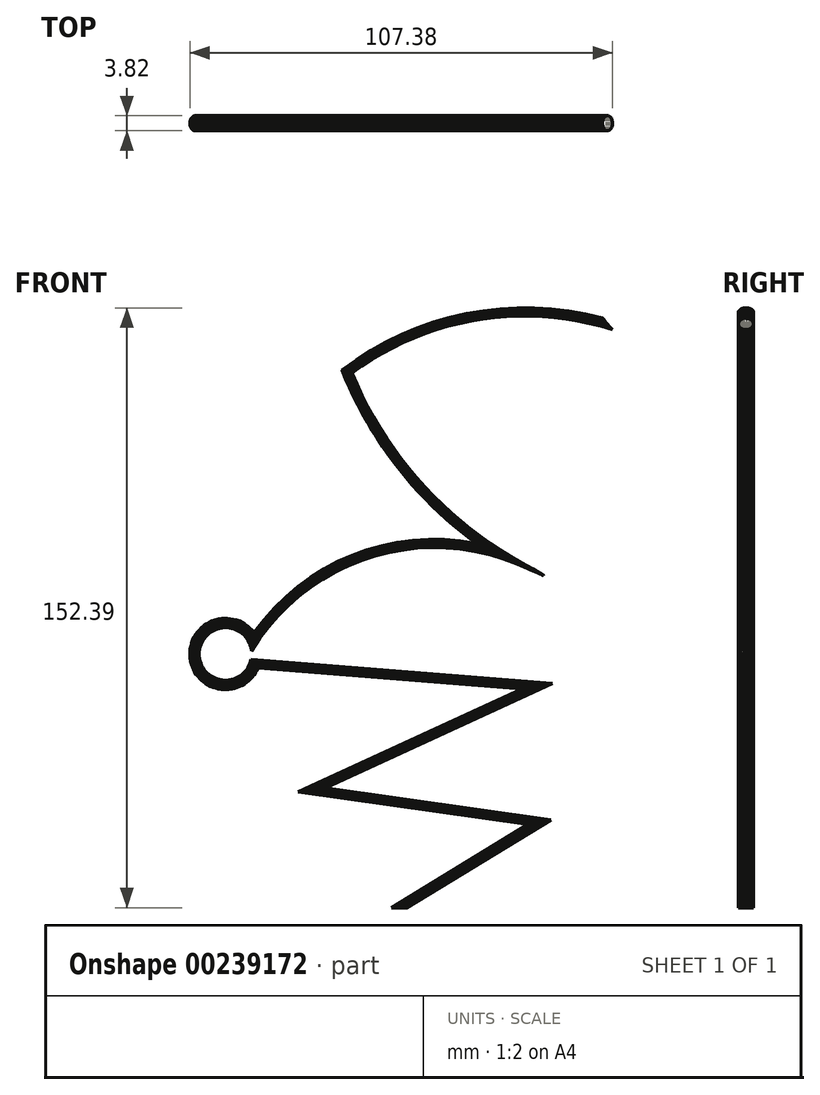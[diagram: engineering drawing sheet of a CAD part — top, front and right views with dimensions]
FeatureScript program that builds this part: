
annotation { "Feature Type Name" : "Feature", "Feature Type Description" : "" }
export const myFeature = defineFeature(function(context is Context, id is Id, definition is map)
    precondition{}
    {
        {
            var Q0;
            Q0=qCreatedBy(makeId("Front.planeOp"),FACE);
            var sketch = newSketch(context, id + "F0", { "sketchPlane" : qUnion([Q0])});
            skLineSegment(sketch, "E0", {"start": v(1.18, 0) * mm, "end": v(37.47, 22.13) * mm});
            skLineSegment(sketch, "E1", {"start": v(37.47, 22.13) * mm, "end": v(-20.03, 30.25) * mm});
            skLineSegment(sketch, "E2", {"start": v(-20.03, 30.25) * mm, "end": v(37.47, 56.77) * mm});
            skLineSegment(sketch, "E3", {"start": v(37.47, 56.77) * mm, "end": v(-37.3, 62.7) * mm});
            skArc(sketch, "E4", {"start": v(30.49, 87.53) * mm, "mid": v(-7.33, 89.4) * mm, "end": v(-37.3, 66.25) * mm});
            skArc(sketch, "E5", {"start": v(-12.47, 136.01) * mm, "mid": v(4.92, 108.15) * mm, "end": v(30.49, 87.53) * mm});
            skArc(sketch, "E6", {"start": v(53.74, 147.44) * mm, "mid": v(19.27, 149.65) * mm, "end": v(-12.47, 136.01) * mm});
            skArc(sketch, "E7", {"start": v(-37.3, 66.25) * mm, "mid": v(-51.15, 64.48) * mm, "end": v(-37.3, 62.7) * mm});
            skSolve(sketch);
        }
        {
            var Q0;
            Q0=qCreatedBy(makeId("Top.planeOp"),FACE);
            var sketch = newSketch(context, id + "F1", { "sketchPlane" : qUnion([Q0])});
            skCircle(sketch, "E8.cCircle", {"center": v(0, 0) * mm, "radius": 1.9 * mm, "construction": true});
            skLineSegment(sketch, "E8.0", {"start": v(0.93, 1.7) * mm, "end": v(1.4, 1.32) * mm});
            skLineSegment(sketch, "E8.1", {"start": v(1.4, 1.32) * mm, "end": v(1.75, 0.82) * mm});
            skLineSegment(sketch, "E8.2", {"start": v(1.75, 0.82) * mm, "end": v(1.91, 0.24) * mm});
            skLineSegment(sketch, "E8.3", {"start": v(1.91, 0.24) * mm, "end": v(1.9, -0.36) * mm});
            skLineSegment(sketch, "E8.4", {"start": v(1.9, -0.36) * mm, "end": v(1.7, -0.93) * mm});
            skLineSegment(sketch, "E8.5", {"start": v(1.7, -0.93) * mm, "end": v(1.32, -1.4) * mm});
            skLineSegment(sketch, "E8.6", {"start": v(1.32, -1.4) * mm, "end": v(0.82, -1.75) * mm});
            skLineSegment(sketch, "E8.7", {"start": v(0.82, -1.75) * mm, "end": v(0.24, -1.91) * mm});
            skLineSegment(sketch, "E8.8", {"start": v(0.24, -1.91) * mm, "end": v(-0.36, -1.9) * mm});
            skLineSegment(sketch, "E8.9", {"start": v(-0.36, -1.9) * mm, "end": v(-0.93, -1.7) * mm});
            skLineSegment(sketch, "E8.10", {"start": v(-0.93, -1.7) * mm, "end": v(-1.4, -1.32) * mm});
            skLineSegment(sketch, "E8.11", {"start": v(-1.4, -1.32) * mm, "end": v(-1.75, -0.82) * mm});
            skLineSegment(sketch, "E8.12", {"start": v(-1.75, -0.82) * mm, "end": v(-1.91, -0.24) * mm});
            skLineSegment(sketch, "E8.13", {"start": v(-1.91, -0.24) * mm, "end": v(-1.9, 0.36) * mm});
            skLineSegment(sketch, "E8.14", {"start": v(-1.9, 0.36) * mm, "end": v(-1.7, 0.93) * mm});
            skLineSegment(sketch, "E8.15", {"start": v(-1.7, 0.93) * mm, "end": v(-1.32, 1.4) * mm});
            skLineSegment(sketch, "E8.16", {"start": v(-1.32, 1.4) * mm, "end": v(-0.82, 1.75) * mm});
            skLineSegment(sketch, "E8.17", {"start": v(-0.82, 1.75) * mm, "end": v(-0.24, 1.91) * mm});
            skLineSegment(sketch, "E8.18", {"start": v(-0.24, 1.91) * mm, "end": v(0.36, 1.9) * mm});
            skLineSegment(sketch, "E8.19", {"start": v(0.36, 1.9) * mm, "end": v(0.93, 1.7) * mm});
            skPoint(sketch, "E8.0.midPoint", {"position": v(1.17, 1.5) * mm});
            skSolve(sketch);
        }
        {
            var Q0;
            Q0 = qSketchRegion(id + "F1", true);
            var Q1;
            Q1 = qConstructionFilter(qBodyType(qCreatedBy(id + "F0" ,EDGE), BodyType.WIRE), ConstructionObject.NO);
            sweep(context, id + "F2", {"profiles" : qUnion([Q0]), "path" : qUnion([Q1])});
        }
    });
